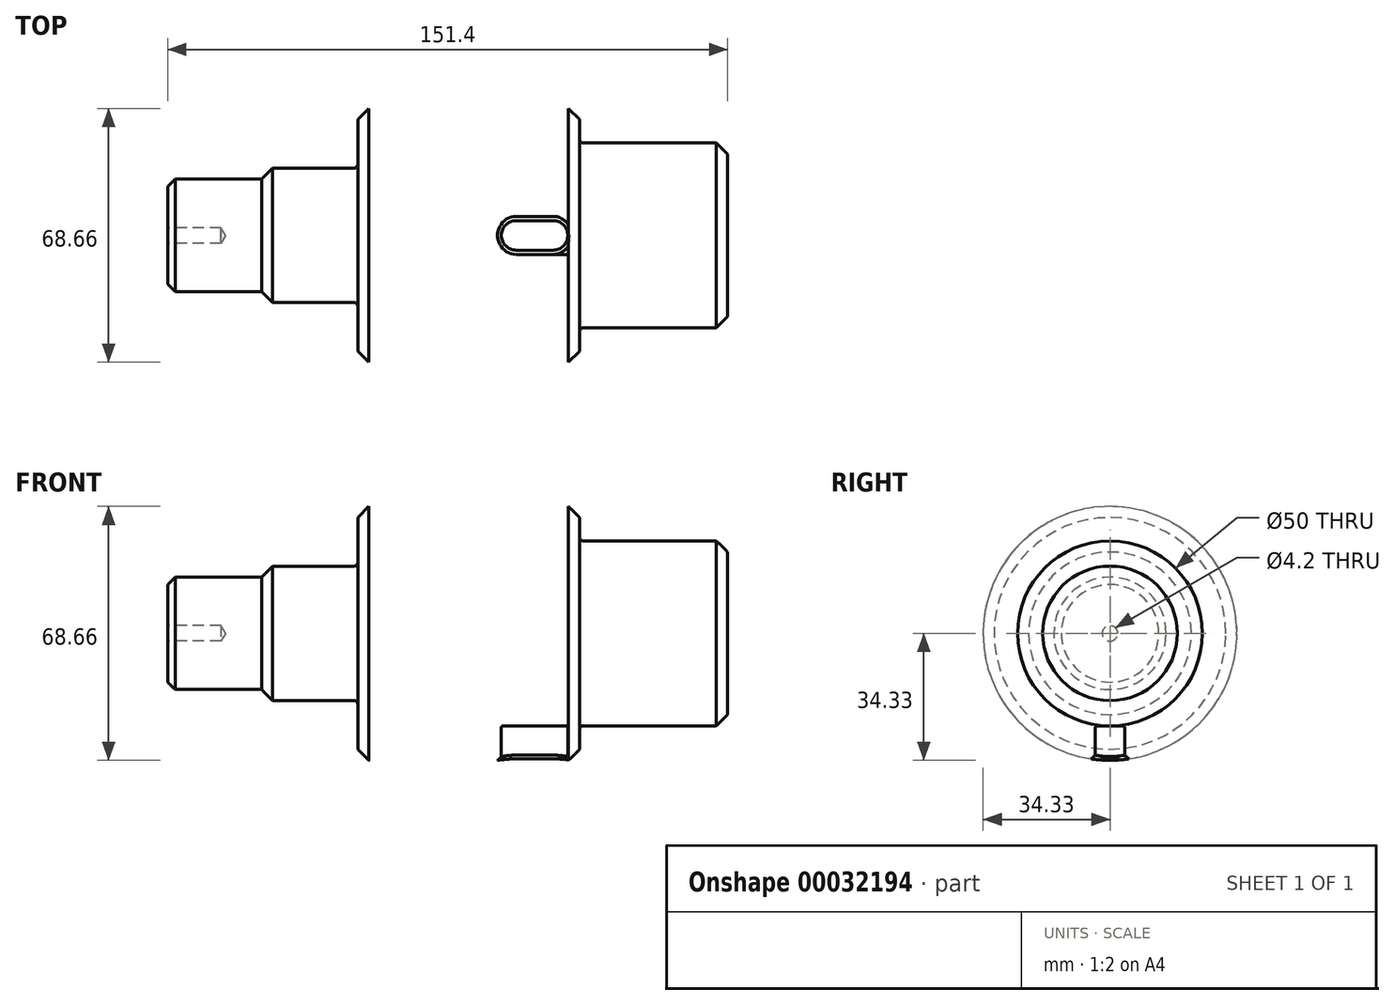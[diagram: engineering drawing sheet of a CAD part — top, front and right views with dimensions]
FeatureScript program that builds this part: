
annotation { "Feature Type Name" : "Feature", "Feature Type Description" : "" }
export const myFeature = defineFeature(function(context is Context, id is Id, definition is map)
    precondition{}
    {
        {
            var Q0;
            Q0=qCreatedBy(makeId("Front.planeOp"),FACE);
            var sketch = newSketch(context, id + "F0", { "sketchPlane" : qUnion([Q0])});
            skLineSegment(sketch, "E0", {"start": v(0, 0) * mm, "end": v(61, 0) * mm});
            skLineSegment(sketch, "E1", {"start": v(61, 0) * mm, "end": v(61, 25) * mm});
            skLineSegment(sketch, "E2", {"start": v(61, 25) * mm, "end": v(21, 25) * mm});
            skLineSegment(sketch, "E3", {"start": v(21, 25) * mm, "end": v(21, 34.33) * mm});
            skLineSegment(sketch, "E4", {"start": v(21, 34.33) * mm, "end": v(-39, 34.33) * mm});
            skLineSegment(sketch, "E5", {"start": v(-39, 34.33) * mm, "end": v(-39, 18.2) * mm});
            skLineSegment(sketch, "E6", {"start": v(-39, 18.2) * mm, "end": v(-65, 18.2) * mm});
            skLineSegment(sketch, "E7", {"start": v(-65, 18.2) * mm, "end": v(-65, 0) * mm});
            skLineSegment(sketch, "E8", {"start": v(-65, 0) * mm, "end": v(0, 0) * mm});
            skSolve(sketch);
        }
        {
            var Q0;
            Q0=makeQuery(id+"F0.imprint","IMPRINT",FACE,{"disambiguationData":[TD([[makeQuery(id+"F0.imprint","IMPRINT",EDGE,{"derivedFrom":sQuery(id+"F0.wireOp",EDGE,"E0")}),1.0]])]});
            var Q1;
            Q1=sQuery(id+"F0.wireOp",EDGE,"E6");
            var Q2;
            Q2=sQuery(id+"F0.wireOp",EDGE,"E7");
            var Q3;
            Q3=sQuery(id+"F0.wireOp",EDGE,"E5");
            var Q4;
            Q4=sQuery(id+"F0.wireOp",EDGE,"E4");
            var Q5;
            Q5=sQuery(id+"F0.wireOp",EDGE,"E3");
            var Q6;
            Q6=sQuery(id+"F0.wireOp",EDGE,"E2");
            var Q7;
            Q7=sQuery(id+"F0.wireOp",EDGE,"E1");
            var Q8;
            Q8=sQuery(id+"F0.wireOp",EDGE,"E8");
            revolve(context, id + "F1", {"entities" : qUnion([Q0]), "surfaceEntities" : qUnion([Q1, Q2, Q3, Q4, Q5, Q6, Q7]), "axis" : qUnion([Q8]), "revolveType" : RevolveType.FULL});
        }
        {
            var Q0;
            Q0=makeQuery(id+"F1.opRevolve","SWEPT_EDGE",EDGE,{"disambiguationData":[OSD([sQuery(id+"F0.wireOp",VERTEX,"E2.end")])]});
            var Q1;
            Q1=makeQuery(id+"F1.opRevolve","SWEPT_EDGE",EDGE,{"disambiguationData":[OSD([sQuery(id+"F0.wireOp",VERTEX,"E5.end")])]});
            var Q2;
            Q2=makeQuery(id+"F1.opRevolve","SWEPT_EDGE",EDGE,{"disambiguationData":[OSD([sQuery(id+"F0.wireOp",EDGE,"E2"),sQuery(id+"F0.wireOp",EDGE,"E3")])]});
            var Q3;
            Q3=makeQuery(id+"F1.opRevolve","SWEPT_EDGE",EDGE,{"disambiguationData":[OSD([sQuery(id+"F0.wireOp",EDGE,"E5"),sQuery(id+"F0.wireOp",EDGE,"E6")])]});
            fillet(context, id + "F2", {"entities" : qUnion([Q0, Q1, Q2, Q3]), "radius" : 1 * mm, "tangentPropagation" : true, "allowEdgeOverflow" : false});
        }
        {
            var Q0;
            Q0=makeQuery(id+"F1.opRevolve","SWEPT_EDGE",EDGE,{"disambiguationData":[OSD([sQuery(id+"F0.wireOp",EDGE,"E4"),sQuery(id+"F0.wireOp",EDGE,"E5")])]});
            var Q1;
            Q1=makeQuery(id+"F1.opRevolve","SWEPT_EDGE",EDGE,{"disambiguationData":[OSD([sQuery(id+"F0.wireOp",EDGE,"E3"),sQuery(id+"F0.wireOp",EDGE,"E4")])]});
            var Q2;
            Q2=makeQuery(id+"F1.opRevolve","SWEPT_EDGE",EDGE,{"disambiguationData":[OSD([sQuery(id+"F0.wireOp",EDGE,"E6"),sQuery(id+"F0.wireOp",EDGE,"E7")])]});
            var Q3;
            Q3=makeQuery(id+"F1.opRevolve","SWEPT_EDGE",EDGE,{"disambiguationData":[OSD([sQuery(id+"F0.wireOp",EDGE,"E1"),sQuery(id+"F0.wireOp",EDGE,"E2")])]});
            chamfer(context, id + "F3", {"entities" : qUnion([Q0, Q1, Q2, Q3]), "width" : 3 * mm, "tangentPropagation" : true});
        }
        {
            var Q0;
            Q0=makeQuery(id+"F1.opRevolve","SWEPT_FACE",FACE,{"disambiguationData":[OSD([sQuery(id+"F0.wireOp",EDGE,"E7")])]});
            extrude(context, id + "F4", {"entities" : qUnion([Q0]), "operationType" : NewBodyOperationType.ADD, "depth" : 25.4 * mm});
        }
        {
            var Q0;
            Q0=makeQuery(id+"F4.opExtrude","CAP_EDGE",EDGE,{"disambiguationData":[OSD([sQuery(id+"F0.wireOp",EDGE,"E6"),sQuery(id+"F0.wireOp",EDGE,"E7")])],"isStart":false});
            chamfer(context, id + "F5", {"entities" : qUnion([Q0]), "width" : 2 * mm, "tangentPropagation" : true});
        }
        {
            var Q0;
            Q0=makeQuery(id+"F4.opExtrude","CAP_FACE",FACE,{"disambiguationData":[OSD([sQuery(id+"F0.wireOp",EDGE,"E7")])],"isStart":false});
            var sketch = newSketch(context, id + "F6", { "sketchPlane" : qUnion([Q0])});
            skCircle(sketch, "E9.0", {"center": v(0, 0) * mm, "radius": 13.2 * mm});
            skSolve(sketch);
        }
        {
            var Q0;
            Q0=sQuery(id+"F6.wireOp",VERTEX,"E9.0.center");
            var Q1;
            Q1=makeQuery(id+"F1.opRevolve","SWEPT_BODY",BODY,{"disambiguationData":[OSD([sQuery(id+"F0.wireOp",EDGE,"E0"),sQuery(id+"F0.wireOp",EDGE,"E1"),sQuery(id+"F0.wireOp",EDGE,"E2"),sQuery(id+"F0.wireOp",EDGE,"E3"),sQuery(id+"F0.wireOp",EDGE,"E4"),sQuery(id+"F0.wireOp",EDGE,"E5"),sQuery(id+"F0.wireOp",EDGE,"E6"),sQuery(id+"F0.wireOp",EDGE,"E7"),sQuery(id+"F0.wireOp",EDGE,"E8")])]});
            hole(context, id + "F7", {"style" : HoleStyle.SIMPLE, "endStyle" : HoleEndStyle.BLIND, "standardTappedOrClearance" : lookupTablePath({ "standard" : "ISO", "engagement" : "75%", "pitch" : "0.8 mm", "size" : "M5", "type" : "Tapped" }), "standardBlindInLast" : lookupTablePath({ "standard" : "ISO", "engagement" : "75%", "pitch" : "0.8 mm", "size" : "M5", "type" : "Tapped" }), "holeDiameter" : 4.2 * mm, "showTappedDepth" : true, "holeDepth" : 14.4 * mm, "isTappedThrough" : true, "tappedDepth" : 12 * mm, "tapClearance" : 3, "startFromSketch" : true, "locations" : qUnion([Q0]), "scope" : qUnion([Q1]), "majorDiameter" : 5 * mm});
        }
        {
            var Q0;
            Q0=qCreatedBy(makeId("Top.planeOp"),FACE);
            var sketch = newSketch(context, id + "F8", { "sketchPlane" : qUnion([Q0])});
            skLineSegment(sketch, "E10", {"start": v(18, -34.33) * mm, "end": v(-36, -34.33) * mm, "construction": true});
            skLineSegment(sketch, "E11", {"start": v(-36, 34.33) * mm, "end": v(18, 34.33) * mm, "construction": true});
            skLineSegment(sketch, "E12", {"start": v(3.83, 4) * mm, "end": v(13.83, 4) * mm});
            skLineSegment(sketch, "E13", {"start": v(13.83, -4) * mm, "end": v(3.83, -4) * mm});
            skArc(sketch, "E14", {"start": v(13.83, 4) * mm, "mid": v(17.83, 0) * mm, "end": v(13.83, -4) * mm});
            skArc(sketch, "E15", {"start": v(3.83, -4) * mm, "mid": v(-0.17, 0) * mm, "end": v(3.83, 4) * mm});
            skSolve(sketch);
        }
        {
            var Q0;
            Q0 = qSketchRegion(id + "F8", true);
            extrude(context, id + "F9", {"entities" : qUnion([Q0]), "operationType" : NewBodyOperationType.REMOVE, "endBound" : BoundingType.UP_TO_NEXT, "oppositeDirection" : true, "depth" : 25 * mm, "hasOffset" : true, "offsetDistance" : 25 * mm, "offsetOppositeDirection" : true, "hasSecondDirection" : true, "secondDirectionOppositeDirection" : true, "secondDirectionDepth" : 25 * mm});
        }
        {
            var Q0;
            Q0=makeQuery(id+"F9.boolean.opBoolean","INTERSECT",EDGE,{"derivedFrom":[makeQuery(id+"F1.opRevolve","SWEPT_FACE",FACE,{"disambiguationData":[OSD([sQuery(id+"F0.wireOp",EDGE,"E4")])]}),makeQuery(id+"F9.opExtrude","SWEPT_FACE",FACE,{"disambiguationData":[OSD([sQuery(id+"F8.wireOp",EDGE,"E13")])]})]});
            chamfer(context, id + "F10", {"entities" : qUnion([Q0]), "width" : 1 * mm, "tangentPropagation" : true});
        }
        {
            var Q0;
            Q0=makeQuery(id+"F9.boolean.opBoolean","COPY",EDGE,{"derivedFrom":makeQuery(id+"F9.opExtrude","CAP_EDGE",EDGE,{"disambiguationData":[OSD([sQuery(id+"F8.wireOp",EDGE,"E15")])],"isStart":true})});
            fillet(context, id + "F11", {"entities" : qUnion([Q0]), "radius" : .5 * mm, "tangentPropagation" : true, "allowEdgeOverflow" : false});
        }
    });
